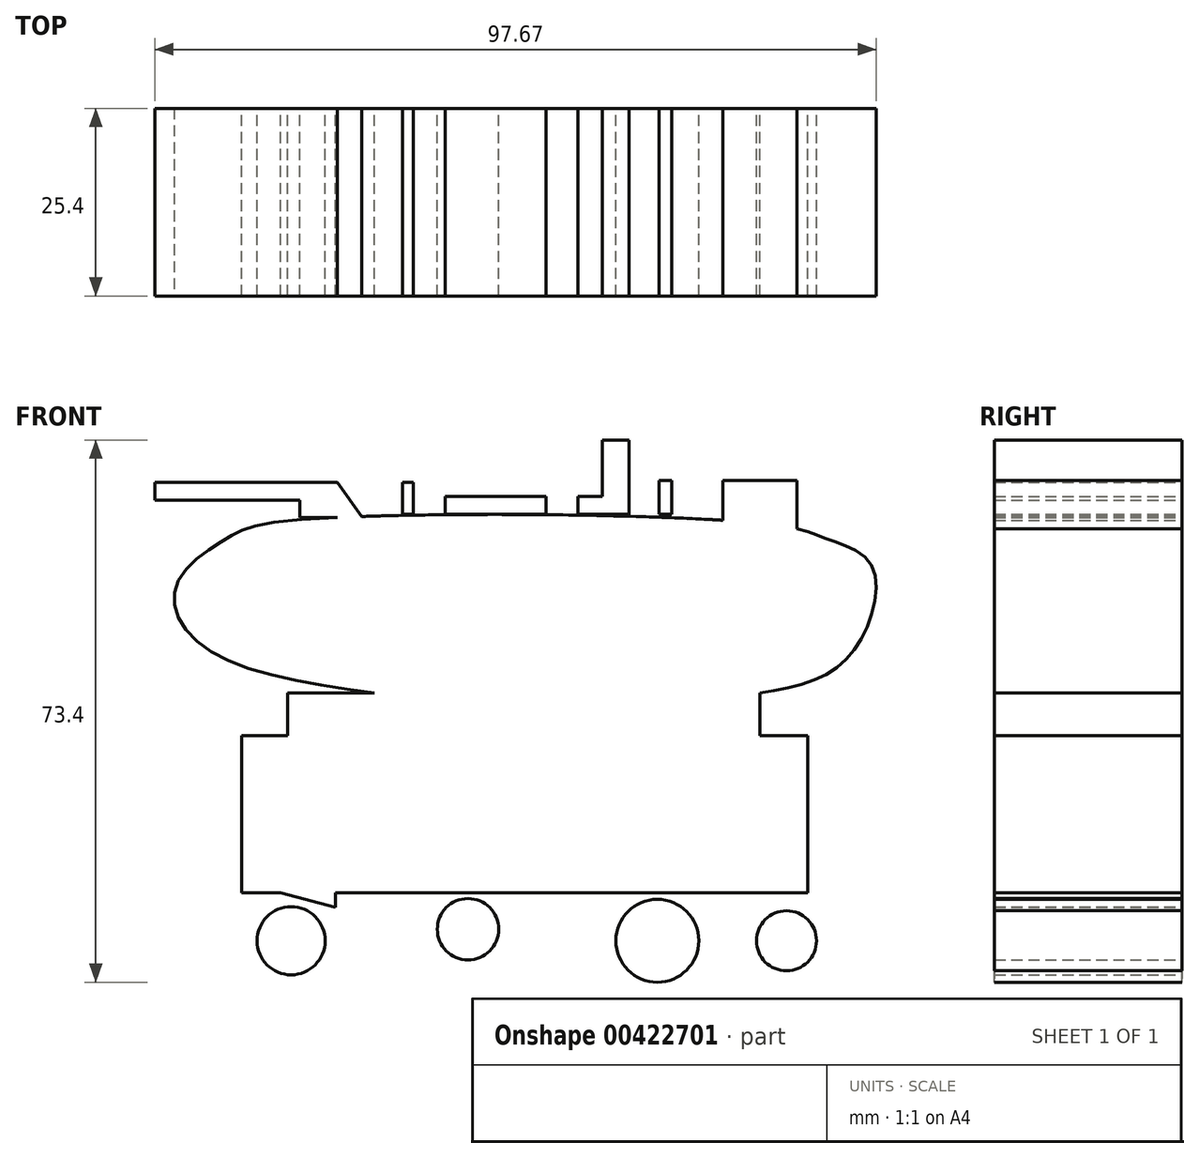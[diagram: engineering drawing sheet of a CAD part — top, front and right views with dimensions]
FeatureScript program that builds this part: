
annotation { "Feature Type Name" : "Feature", "Feature Type Description" : "" }
export const myFeature = defineFeature(function(context is Context, id is Id, definition is map)
    precondition{}
    {
        {
            var Q0;
            Q0=qCreatedBy(makeId("Front.planeOp"),FACE);
            var sketch = newSketch(context, id + "F0", { "sketchPlane" : qUnion([Q0])});
            skLineSegment(sketch, "E0.bottom", {"start": v(35.45, -12.94) * mm, "end": v(-41.2, -12.94) * mm});
            skLineSegment(sketch, "E0.top", {"start": v(35.45, 8.38) * mm, "end": v(-41.2, 8.38) * mm});
            skLineSegment(sketch, "E0.left", {"start": v(35.45, -12.94) * mm, "end": v(35.45, 8.38) * mm});
            skLineSegment(sketch, "E0.right", {"start": v(-41.2, -12.94) * mm, "end": v(-41.2, 8.38) * mm});
            skLineSegment(sketch, "E1.bottom", {"start": v(-34.97, 8.38) * mm, "end": v(28.99, 8.38) * mm});
            skLineSegment(sketch, "E1.top", {"start": v(-34.97, 14.13) * mm, "end": v(28.99, 14.13) * mm});
            skLineSegment(sketch, "E1.left", {"start": v(-34.97, 8.38) * mm, "end": v(-34.97, 14.13) * mm});
            skLineSegment(sketch, "E1.right", {"start": v(28.99, 8.38) * mm, "end": v(28.99, 14.13) * mm});
            skFitSpline(sketch, "E2", {"points": [v(-23.24, 14.13) * mm, v(-43.84, 18.92) * mm, v(-50.07, 25.15) * mm, v(-49.1, 30.42) * mm, v(-43.36, 34.97) * mm, v(-35.7, 37.37) * mm, v(31.14, 36.9) * mm, v(38.09, 34.97) * mm, v(43.84, 31.86) * mm, v(43.84, 23.96) * mm, v(38.57, 17) * mm, v(28.99, 14.13) * mm], "startDerivative": vector(-190.76, 27.48) * mm, "endDerivative": vector(-124.26, -21.73) * mm});
            skLineSegment(sketch, "E3", {"start": v(-35.93, -12.94) * mm, "end": v(-44.32, -22.76) * mm});
            skLineSegment(sketch, "E4", {"start": v(-35.93, -12.94) * mm, "end": v(-28.5, -14.85) * mm});
            skLineSegment(sketch, "E5", {"start": v(-28.5, -15.1) * mm, "end": v(-25.15, -22.76) * mm});
            skLineSegment(sketch, "E6", {"start": v(-28.5, -14.85) * mm, "end": v(-28.5, -12.94) * mm});
            skLineSegment(sketch, "E7", {"start": v(-14.61, -12.94) * mm, "end": v(-19.64, -22.76) * mm});
            skLineSegment(sketch, "E8", {"start": v(-6.47, -12.94) * mm, "end": v(0, -22.76) * mm});
            skLineSegment(sketch, "E9", {"start": v(9.82, -12.94) * mm, "end": v(4.8, -22.76) * mm});
            skLineSegment(sketch, "E10", {"start": v(19.4, -12.94) * mm, "end": v(24.2, -22.76) * mm});
            skLineSegment(sketch, "E11", {"start": v(28.99, -12.94) * mm, "end": v(26.35, -22.76) * mm});
            skLineSegment(sketch, "E12", {"start": v(35.45, -12.94) * mm, "end": v(41.44, -22.76) * mm});
            skCircle(sketch, "E13", {"center": v(-34.5, -19.4) * mm, "radius": 4.6 * mm});
            skCircle(sketch, "E14", {"center": v(-10.54, -17.85) * mm, "radius": 4.16 * mm});
            skPoint(sketch, "E14.centerSnap0", {"position": v(-3.23, -17.85) * mm});
            skCircle(sketch, "E15", {"center": v(15.1, -19.4) * mm, "radius": 5.6 * mm});
            skCircle(sketch, "E16", {"center": v(32.58, -19.4) * mm, "radius": 4.07 * mm});
            skLineSegment(sketch, "E17", {"start": v(-21.32, 38.14) * mm, "end": v(-21.32, 44.38) * mm});
            skLineSegment(sketch, "E18", {"start": v(-7.9, 38.3) * mm, "end": v(-7.9, 49.98) * mm});
            skLineSegment(sketch, "E19", {"start": v(-7.9, 44.14) * mm, "end": v(-13.9, 44.14) * mm});
            skLineSegment(sketch, "E20", {"start": v(-14.13, 44.56) * mm, "end": v(-14.13, 38.27) * mm});
            skLineSegment(sketch, "E21", {"start": v(0, 38.27) * mm, "end": v(0, 44.14) * mm});
            skLineSegment(sketch, "E22", {"start": v(12.2, 38.03) * mm, "end": v(12.2, 47.23) * mm});
            skLineSegment(sketch, "E23", {"start": v(12.2, 47.23) * mm, "end": v(21.56, 47.23) * mm});
            skLineSegment(sketch, "E24", {"start": v(21.8, 47.2) * mm, "end": v(21.8, 35.7) * mm});
            skLineSegment(sketch, "E25.bottom", {"start": v(-28.23, 37.9) * mm, "end": v(-33.3, 37.9) * mm});
            skLineSegment(sketch, "E25.top", {"start": v(-28.23, 40.26) * mm, "end": v(-33.3, 40.26) * mm});
            skLineSegment(sketch, "E25.left", {"start": v(-28.23, 37.9) * mm, "end": v(-28.23, 40.26) * mm});
            skLineSegment(sketch, "E25.right", {"start": v(-33.3, 37.9) * mm, "end": v(-33.3, 40.26) * mm});
            skLineSegment(sketch, "E26.bottom", {"start": v(-28.23, 40.26) * mm, "end": v(-52.94, 40.26) * mm});
            skLineSegment(sketch, "E26.top", {"start": v(-28.23, 42.64) * mm, "end": v(-52.94, 42.64) * mm});
            skLineSegment(sketch, "E26.left", {"start": v(-28.23, 40.26) * mm, "end": v(-28.23, 42.64) * mm});
            skLineSegment(sketch, "E26.right", {"start": v(-52.94, 40.26) * mm, "end": v(-52.94, 42.64) * mm});
            skLineSegment(sketch, "E27", {"start": v(-28.23, 42.64) * mm, "end": v(-24.9, 38.03) * mm});
            skLineSegment(sketch, "E28", {"start": v(-28.23, 40.26) * mm, "end": v(-28.23, 37.9) * mm});
            skLineSegment(sketch, "E29", {"start": v(-28.23, 40.26) * mm, "end": v(-24.9, 38.03) * mm});
            skSolve(sketch);
        }
        {
            var Q0;
            Q0 = qSketchRegion(id + "F0", true);
            extrude(context, id + "F1", {"entities" : qUnion([Q0]), "depth" : 25.4 * mm});
        }
        {
            var Q0;
            Q0=qCreatedBy(makeId("Front.planeOp"),FACE);
            var sketch = newSketch(context, id + "F2", { "sketchPlane" : qUnion([Q0])});
            skLineSegment(sketch, "E30.bottom", {"start": v(-12.22, 38.33) * mm, "end": v(-13.65, 38.33) * mm});
            skLineSegment(sketch, "E31.bottom", {"start": v(-17.97, 38.33) * mm, "end": v(-19.4, 38.33) * mm});
            skLineSegment(sketch, "E31.top", {"start": v(-17.97, 42.64) * mm, "end": v(-19.4, 42.64) * mm});
            skLineSegment(sketch, "E31.left", {"start": v(-17.97, 38.33) * mm, "end": v(-17.97, 42.64) * mm});
            skLineSegment(sketch, "E31.right", {"start": v(-19.4, 38.33) * mm, "end": v(-19.4, 42.64) * mm});
            skPoint(sketch, "E32.bottom.start.orphan", {"position": v(-6.47, 38.33) * mm});
            skLineSegment(sketch, "E33.bottom", {"start": v(-13.65, 38.33) * mm, "end": v(0, 38.33) * mm});
            skLineSegment(sketch, "E33.top", {"start": v(-13.65, 40.72) * mm, "end": v(0, 40.72) * mm});
            skLineSegment(sketch, "E33.left", {"start": v(-13.65, 38.33) * mm, "end": v(-13.65, 40.72) * mm});
            skLineSegment(sketch, "E33.right", {"start": v(0, 38.33) * mm, "end": v(0, 40.72) * mm});
            skLineSegment(sketch, "E34.bottom", {"start": v(7.67, 38.33) * mm, "end": v(4.31, 38.33) * mm});
            skLineSegment(sketch, "E34.top", {"start": v(7.67, 40.72) * mm, "end": v(4.31, 40.72) * mm});
            skLineSegment(sketch, "E34.left", {"start": v(7.67, 38.33) * mm, "end": v(7.67, 40.72) * mm});
            skLineSegment(sketch, "E34.right", {"start": v(4.31, 38.33) * mm, "end": v(4.31, 40.72) * mm});
            skLineSegment(sketch, "E35.bottom", {"start": v(11.26, 38.33) * mm, "end": v(7.67, 38.33) * mm});
            skLineSegment(sketch, "E35.top", {"start": v(11.26, 48.39) * mm, "end": v(7.67, 48.39) * mm});
            skLineSegment(sketch, "E35.left", {"start": v(11.26, 38.33) * mm, "end": v(11.26, 48.39) * mm});
            skLineSegment(sketch, "E35.right", {"start": v(7.67, 38.33) * mm, "end": v(7.67, 48.39) * mm});
            skLineSegment(sketch, "E36.bottom", {"start": v(34.02, 36.17) * mm, "end": v(23.96, 36.17) * mm});
            skLineSegment(sketch, "E36.top", {"start": v(34.02, 42.88) * mm, "end": v(23.96, 42.88) * mm});
            skLineSegment(sketch, "E36.left", {"start": v(34.02, 36.17) * mm, "end": v(34.02, 42.88) * mm});
            skLineSegment(sketch, "E36.right", {"start": v(23.96, 36.17) * mm, "end": v(23.96, 42.88) * mm});
            skLineSegment(sketch, "E37.bottom", {"start": v(15.33, 38.33) * mm, "end": v(17, 38.33) * mm});
            skLineSegment(sketch, "E37.top", {"start": v(15.33, 42.88) * mm, "end": v(17, 42.88) * mm});
            skLineSegment(sketch, "E37.left", {"start": v(15.33, 38.33) * mm, "end": v(15.33, 42.88) * mm});
            skLineSegment(sketch, "E37.right", {"start": v(17, 38.33) * mm, "end": v(17, 42.88) * mm});
            skSolve(sketch);
        }
        {
            var Q0;
            Q0 = qSketchRegion(id + "F2", true);
            extrude(context, id + "F3", {"entities" : qUnion([Q0]), "operationType" : NewBodyOperationType.ADD, "depth" : 25.4 * mm});
        }
        {
            var Q0;
            Q0=qCreatedBy(makeId("Front.planeOp"),FACE);
            var Q1;
            Q1 = qBodyType(qCreatedBy(id + "F5" ,EDGE), BodyType.WIRE);
            cPlane(context, id + "F4", {"entities" : qUnion([Q0, Q1]), "cplaneType" : CPlaneType.OFFSET, "offset" : 25.4 * mm, "width" : 152.4 * mm, "height" : 152.4 * mm});
        }
    });
